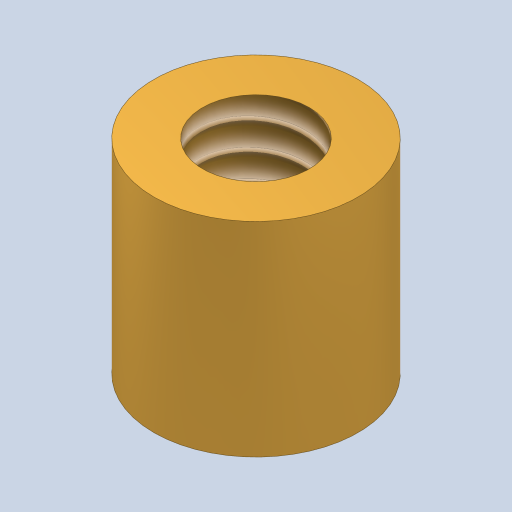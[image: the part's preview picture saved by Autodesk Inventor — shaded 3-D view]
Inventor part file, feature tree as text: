
AUTODESK INVENTOR PART (.ipt)
format: ipt  version: 2023 (Build 270158000, 158)  size: 148,992 bytes
history: native  units: in
note: dims shown in document units (in); Inventor stores cm internally (conversion verified against a paired STEP export)
features: other x1, sketch x1, extrude x1, hole x1
ambient origin geometry x8: Origin, YZ Plane, XZ Plane, XY Plane, X Axis, Y Axis, Z Axis, Center Point
bodies: Body1 (feature_tree)
feature tree (4):
  other  "ソリッド1"
  sketch  "スケッチ1"
  extrude  "押し出し1"  Depth=0.1181in
  hole  "穴1"  [1 undecoded]
note: 1 required parameter value undecoded (feature->parameter linkage not recoverable at this tier; creation-order binding heuristic only, values carry confidence <= 0.55)
